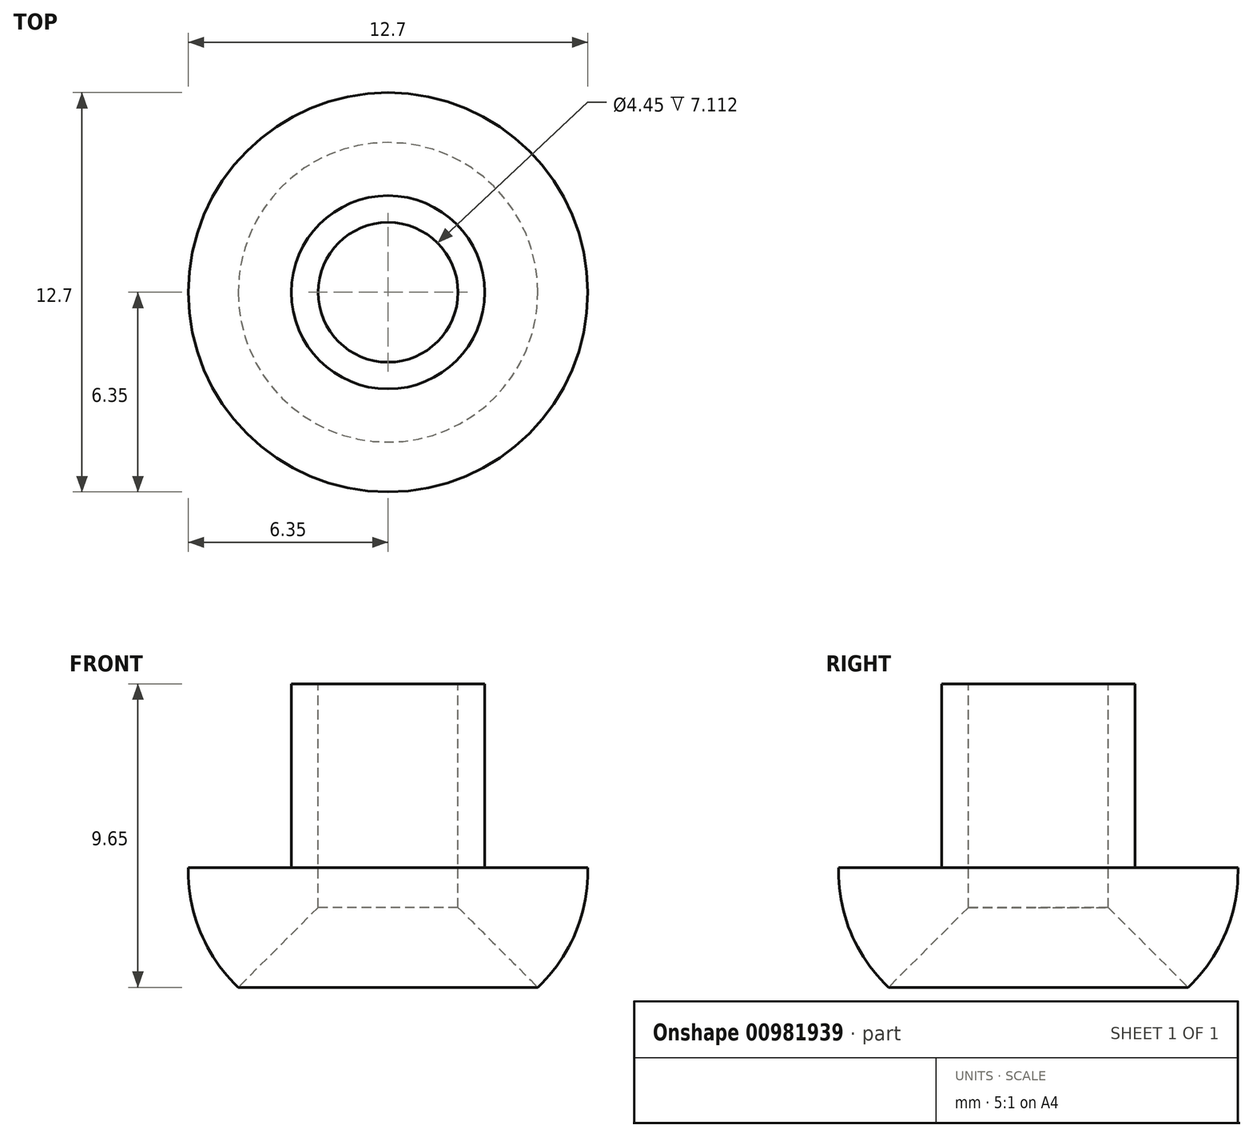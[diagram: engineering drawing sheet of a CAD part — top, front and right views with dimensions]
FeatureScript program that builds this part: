
annotation { "Feature Type Name" : "Feature", "Feature Type Description" : "" }
export const myFeature = defineFeature(function(context is Context, id is Id, definition is map)
    precondition{}
    {
        {
            var Q0;
            Q0=qCreatedBy(makeId("Top.planeOp"),FACE);
            var sketch = newSketch(context, id + "F0", { "sketchPlane" : qUnion([Q0])});
            skCircle(sketch, "E0", {"center": v(0, 0) * mm, "radius": 6.35 * mm});
            skSolve(sketch);
        }
        {
            var Q0;
            Q0=qSketchRegion(id+"F0",true);
            extrude(context, id + "F1", {"entities" : qUnion([Q0]), "depth" : 3.8 * mm, "offsetDistance" : 25.4 * mm});
        }
        {
            var Q0;
            Q0=makeQuery(id+"F1.opExtrude","CAP_FACE",FACE,{"disambiguationData":[OSD([sQuery(id+"F0.wireOp",EDGE,"E0")])],"isStart":false});
            var sketch = newSketch(context, id + "F2", { "sketchPlane" : qUnion([Q0])});
            skCircle(sketch, "E1", {"center": v(0, 0) * mm, "radius": 3.07 * mm});
            skSolve(sketch);
        }
        {
            var Q0;
            Q0=qSketchRegion(id+"F2",true);
            extrude(context, id + "F3", {"entities" : qUnion([Q0]), "operationType" : NewBodyOperationType.ADD, "depth" : 5.84 * mm, "offsetDistance" : 25.4 * mm});
        }
        {
            var Q0;
            Q0=makeQuery(id+"F3.opExtrude","CAP_FACE",FACE,{"disambiguationData":[OSD([sQuery(id+"F2.wireOp",EDGE,"E1")])],"isStart":false});
            var sketch = newSketch(context, id + "F4", { "sketchPlane" : qUnion([Q0])});
            skCircle(sketch, "E2", {"center": v(0, 0) * mm, "radius": 2.22 * mm});
            skSolve(sketch);
        }
        {
            var Q0;
            Q0=qSketchRegion(id+"F4",true);
            extrude(context, id + "F5", {"entities" : qUnion([Q0]), "operationType" : NewBodyOperationType.REMOVE, "endBound" : BoundingType.THROUGH_ALL, "oppositeDirection" : true, "depth" : 25.4 * mm, "offsetDistance" : 25.4 * mm});
        }
        {
            var Q0;
            Q0=makeQuery(id+"F5.boolean.opBoolean","INTERSECT",EDGE,{"derivedFrom":[makeQuery(id+"F1.opExtrude","CAP_FACE",FACE,{"disambiguationData":[OSD([sQuery(id+"F0.wireOp",EDGE,"E0")])],"isStart":true}),makeQuery(id+"F5.opExtrude","SWEPT_FACE",FACE,{"disambiguationData":[OSD([sQuery(id+"F4.wireOp",EDGE,"E2")])]})]});
            chamfer(context, id + "F6", {"entities" : qUnion([Q0]), "chamferType" : ChamferType.OFFSET_ANGLE, "width" : 2.54 * mm, "oppositeDirection" : false, "angle" : 45 * degree, "tangentPropagation" : true});
        }
        {
            var Q0;
            Q0=makeQuery(id+"F1.opExtrude","CAP_EDGE",EDGE,{"disambiguationData":[OSD([sQuery(id+"F0.wireOp",EDGE,"E0")])],"isStart":true});
            fillet(context, id + "F7", {"entities" : qUnion([Q0]), "radius" : 5.08 * mm, "tangentPropagation" : true, "allowEdgeOverflow" : false});
        }
    });
